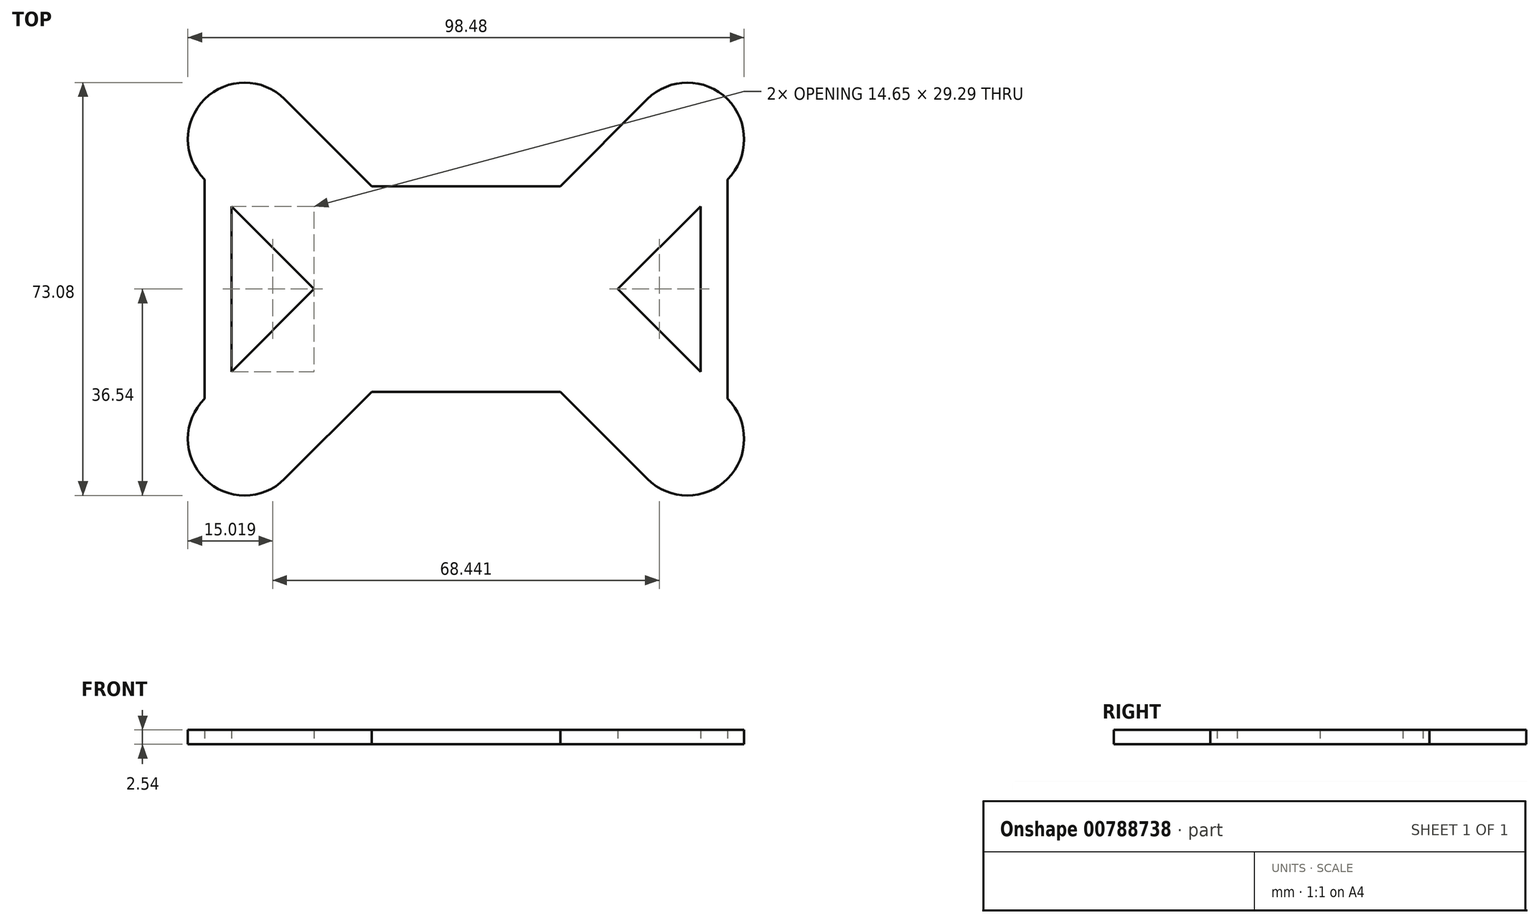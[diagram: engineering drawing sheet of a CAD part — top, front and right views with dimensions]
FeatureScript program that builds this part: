
annotation { "Feature Type Name" : "Feature", "Feature Type Description" : "" }
export const myFeature = defineFeature(function(context is Context, id is Id, definition is map)
    precondition{}
    {
        {
            var Q0;
            Q0=qCreatedBy(makeId("Top.planeOp"),FACE);
            var sketch = newSketch(context, id + "F0", { "sketchPlane" : qUnion([Q0])});
            skPoint(sketch, "E0.middle", {"position": v(0, 0) * mm});
            skPoint(sketch, "E1", {"position": v(0, 18.2) * mm});
            skPoint(sketch, "E2.1.0", {"position": v(-12.88, 12.88) * mm});
            skPoint(sketch, "E2.2.0", {"position": v(-18.2, 0) * mm});
            skPoint(sketch, "E2.3.0", {"position": v(-12.88, -12.88) * mm});
            skPoint(sketch, "E2.4.0", {"position": v(0, -18.2) * mm});
            skPoint(sketch, "E2.5.0", {"position": v(12.88, -12.88) * mm});
            skPoint(sketch, "E2.6.0", {"position": v(18.2, 0) * mm});
            skPoint(sketch, "E2.7.0", {"position": v(12.88, 12.88) * mm});
            skCircle(sketch, "E3", {"center": v(-39.2, 26.5) * mm, "radius": 10.04 * mm});
            skLineSegment(sketch, "E4", {"start": v(-11.2, 12.7) * mm, "end": v(-32.1, 33.6) * mm});
            skLineSegment(sketch, "E5.MirrorCS", {"start": v(11.2, 12.7) * mm, "end": v(32.1, 33.6) * mm});
            skCircle(sketch, "E6.MirrorC", {"center": v(39.2, 26.5) * mm, "radius": 10.04 * mm});
            skCircle(sketch, "E7.MirrorC", {"center": v(-39.2, -26.5) * mm, "radius": 10.04 * mm});
            skLineSegment(sketch, "E8.MirrorCS", {"start": v(-11.2, -12.7) * mm, "end": v(-32.1, -33.6) * mm});
            skLineSegment(sketch, "E9.MirrorCS", {"start": v(11.2, -12.7) * mm, "end": v(32.1, -33.6) * mm});
            skCircle(sketch, "E10.MirrorC", {"center": v(39.2, -26.5) * mm, "radius": 10.04 * mm});
            skLineSegment(sketch, "E11", {"start": v(0, 18.2) * mm, "end": v(16.71, 18.2) * mm});
            skLineSegment(sketch, "E12", {"start": v(16.71, 18.2) * mm, "end": v(-16.71, 18.2) * mm});
            skLineSegment(sketch, "E13.MirrorCS", {"start": v(16.71, -18.2) * mm, "end": v(-16.71, -18.2) * mm});
            skLineSegment(sketch, "E14", {"start": v(41.54, 14.65) * mm, "end": v(41.54, -14.65) * mm});
            skLineSegment(sketch, "E15", {"start": v(46.3, -19.4) * mm, "end": v(46.3, 19.4) * mm});
            skLineSegment(sketch, "E16", {"start": v(41.54, 14.65) * mm, "end": v(26.9, 0) * mm});
            skLineSegment(sketch, "E17", {"start": v(26.9, 0) * mm, "end": v(41.54, -14.65) * mm});
            skLineSegment(sketch, "E18.MirrorCS", {"start": v(-41.54, 14.65) * mm, "end": v(-41.54, -14.65) * mm});
            skLineSegment(sketch, "E19.MirrorCS", {"start": v(-41.54, 14.65) * mm, "end": v(-26.9, 0) * mm});
            skLineSegment(sketch, "E20.MirrorCS", {"start": v(-26.9, 0) * mm, "end": v(-41.54, -14.65) * mm});
            skLineSegment(sketch, "E21.MirrorCS", {"start": v(-46.3, -19.4) * mm, "end": v(-46.3, 19.4) * mm});
            skSolve(sketch);
        }
        {
            var Q0;
            Q0 = qSketchRegion(id + "F0", true);
            extrude(context, id + "F1", {"entities" : qUnion([Q0]), "depth" : 2.54 * mm, "offsetDistance" : 25.4 * mm});
        }
    });
